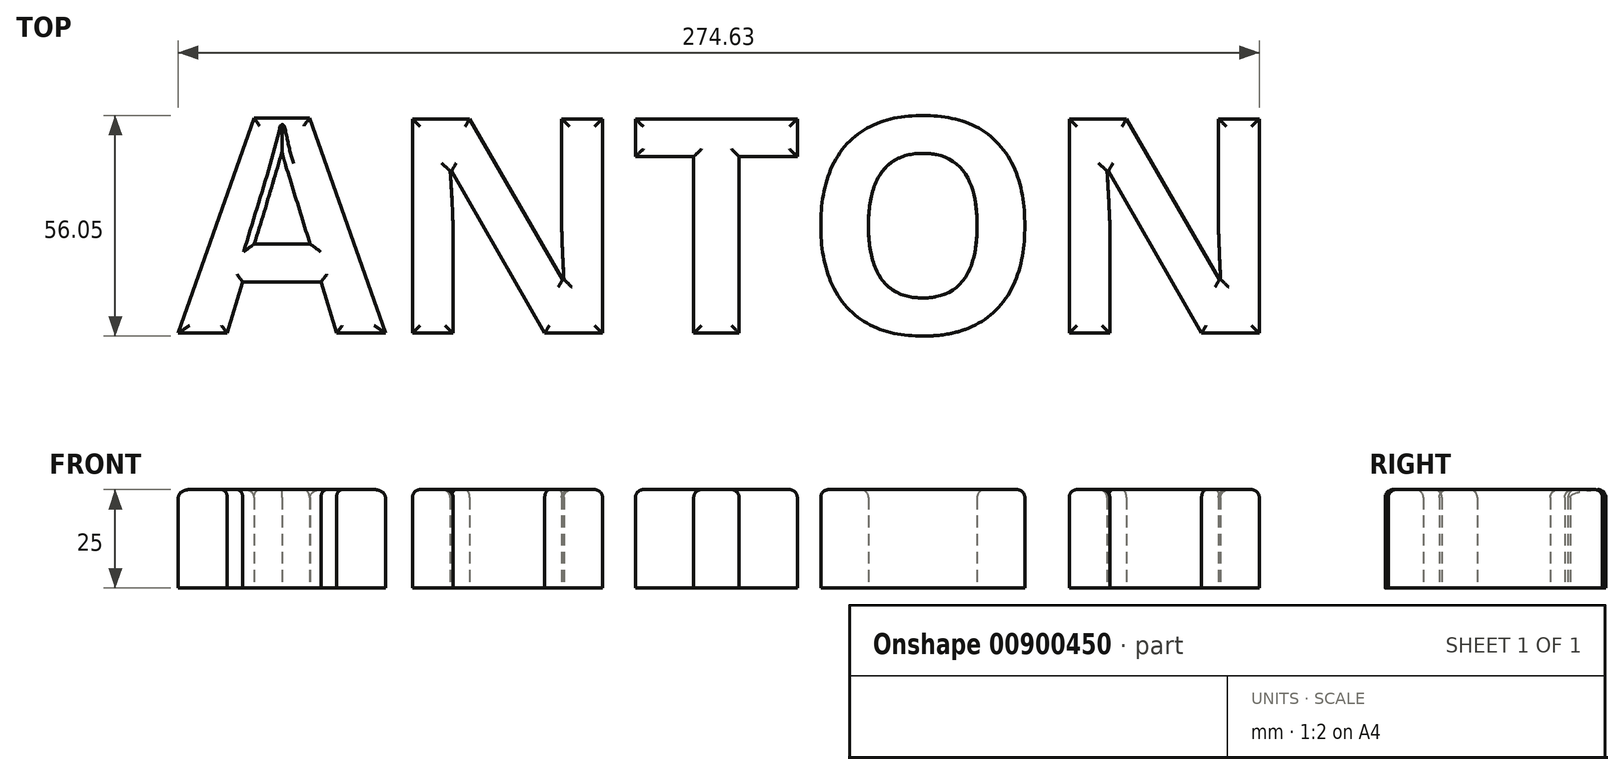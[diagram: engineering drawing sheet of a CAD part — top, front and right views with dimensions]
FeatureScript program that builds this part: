
annotation { "Feature Type Name" : "Feature", "Feature Type Description" : "" }
export const myFeature = defineFeature(function(context is Context, id is Id, definition is map)
    precondition{}
    {
        {
            var Q0;
            Q0=qCreatedBy(makeId("Top.planeOp"),FACE);
            var sketch = newSketch(context, id + "F0", { "sketchPlane" : qUnion([Q0])});
            skText(sketch, "E0", { "text": "ANTON", "fontName": "OpenSans-Bold.ttf"});
            const initialGuessF0  = {"E0": [-0.1224, -0.01433, 1, 0, 0.05491]};
            skSetInitialGuess(sketch, initialGuessF0);
            skSolve(sketch);
        }
        {
            var Q0;
            Q0 = qSketchRegion(id + "F0", true);
            extrude(context, id + "F1", {"entities" : qUnion([Q0]), "depth" : 25 * mm, "offsetDistance" : 25 * mm});
        }
        {
            var Q0;
            Q0=makeQuery(id+"F1.opExtrude","CAP_EDGE",EDGE,{"disambiguationData":[OSD([sQuery(id+"F0.wireOp",EDGE,"E0.sketch_text.stroke-49")])],"isStart":false});
            var Q1;
            Q1=makeQuery(id+"F1.opExtrude","CAP_EDGE",EDGE,{"disambiguationData":[OSD([sQuery(id+"F0.wireOp",EDGE,"E0.sketch_text.stroke-52")])],"isStart":false});
            var Q2;
            Q2=makeQuery(id+"F1.opExtrude","CAP_EDGE",EDGE,{"disambiguationData":[OSD([sQuery(id+"F0.wireOp",EDGE,"E0.sketch_text.stroke-48")])],"isStart":false});
            var Q3;
            Q3=makeQuery(id+"F1.opExtrude","CAP_EDGE",EDGE,{"disambiguationData":[OSD([sQuery(id+"F0.wireOp",EDGE,"E0.sketch_text.stroke-53")])],"isStart":false});
            var Q4;
            Q4=makeQuery(id+"F1.opExtrude","CAP_EDGE",EDGE,{"disambiguationData":[OSD([sQuery(id+"F0.wireOp",EDGE,"E0.sketch_text.stroke-36")])],"isStart":false});
            var Q5;
            Q5=makeQuery(id+"F1.opExtrude","CAP_EDGE",EDGE,{"disambiguationData":[OSD([sQuery(id+"F0.wireOp",EDGE,"E0.sketch_text.stroke-35")])],"isStart":false});
            var Q6;
            Q6=makeQuery(id+"F1.opExtrude","CAP_EDGE",EDGE,{"disambiguationData":[OSD([sQuery(id+"F0.wireOp",EDGE,"E0.sketch_text.stroke-37")])],"isStart":false});
            var Q7;
            Q7=makeQuery(id+"F1.opExtrude","CAP_EDGE",EDGE,{"disambiguationData":[OSD([sQuery(id+"F0.wireOp",EDGE,"E0.sketch_text.stroke-34")])],"isStart":false});
            var Q8;
            Q8=makeQuery(id+"F1.opExtrude","CAP_EDGE",EDGE,{"disambiguationData":[OSD([sQuery(id+"F0.wireOp",EDGE,"E0.sketch_text.stroke-25")])],"isStart":false});
            var Q9;
            Q9=makeQuery(id+"F1.opExtrude","CAP_EDGE",EDGE,{"disambiguationData":[OSD([sQuery(id+"F0.wireOp",EDGE,"E0.sketch_text.stroke-12")])],"isStart":false});
            var Q10;
            Q10=makeQuery(id+"F1.opExtrude","CAP_EDGE",EDGE,{"disambiguationData":[OSD([sQuery(id+"F0.wireOp",EDGE,"E0.sketch_text.stroke-13")])],"isStart":false});
            var Q11;
            Q11=makeQuery(id+"F1.opExtrude","CAP_EDGE",EDGE,{"disambiguationData":[OSD([sQuery(id+"F0.wireOp",EDGE,"E0.sketch_text.stroke-16")])],"isStart":false});
            var Q12;
            Q12=makeQuery(id+"F1.opExtrude","CAP_EDGE",EDGE,{"disambiguationData":[OSD([sQuery(id+"F0.wireOp",EDGE,"E0.sketch_text.stroke-17")])],"isStart":false});
            var Q13;
            Q13=makeQuery(id+"F1.opExtrude","CAP_EDGE",EDGE,{"disambiguationData":[OSD([sQuery(id+"F0.wireOp",EDGE,"E0.sketch_text.stroke-3")])],"isStart":false});
            var Q14;
            Q14=makeQuery(id+"F1.opExtrude","CAP_EDGE",EDGE,{"disambiguationData":[OSD([sQuery(id+"F0.wireOp",EDGE,"E0.sketch_text.stroke-2")])],"isStart":false});
            var Q15;
            Q15=makeQuery(id+"F1.opExtrude","CAP_EDGE",EDGE,{"disambiguationData":[OSD([sQuery(id+"F0.wireOp",EDGE,"E0.sketch_text.stroke-7")])],"isStart":false});
            var Q16;
            Q16=makeQuery(id+"F1.opExtrude","CAP_EDGE",EDGE,{"disambiguationData":[OSD([sQuery(id+"F0.wireOp",EDGE,"E0.sketch_text.stroke-0")])],"isStart":false});
            var Q17;
            Q17=makeQuery(id+"F1.opExtrude","CAP_EDGE",EDGE,{"disambiguationData":[OSD([sQuery(id+"F0.wireOp",EDGE,"E0.sketch_text.stroke-1")])],"isStart":false});
            var Q18;
            Q18=makeQuery(id+"F1.opExtrude","CAP_EDGE",EDGE,{"disambiguationData":[OSD([sQuery(id+"F0.wireOp",EDGE,"E0.sketch_text.stroke-28")])],"isStart":false});
            var Q19;
            Q19=makeQuery(id+"F1.opExtrude","CAP_EDGE",EDGE,{"disambiguationData":[OSD([sQuery(id+"F0.wireOp",EDGE,"E0.sketch_text.stroke-32")])],"isStart":false});
            var Q20;
            Q20=makeQuery(id+"F1.opExtrude","CAP_EDGE",EDGE,{"disambiguationData":[OSD([sQuery(id+"F0.wireOp",EDGE,"E0.sketch_text.stroke-26")])],"isStart":false});
            var Q21;
            Q21=makeQuery(id+"F1.opExtrude","CAP_EDGE",EDGE,{"disambiguationData":[OSD([sQuery(id+"F0.wireOp",EDGE,"E0.sketch_text.stroke-31")])],"isStart":false});
            var Q22;
            Q22=makeQuery(id+"F1.opExtrude","CAP_EDGE",EDGE,{"disambiguationData":[OSD([sQuery(id+"F0.wireOp",EDGE,"E0.sketch_text.stroke-33")])],"isStart":false});
            var Q23;
            Q23=makeQuery(id+"F1.opExtrude","CAP_EDGE",EDGE,{"disambiguationData":[OSD([sQuery(id+"F0.wireOp",EDGE,"E0.sketch_text.stroke-54")])],"isStart":false});
            var Q24;
            Q24=makeQuery(id+"F1.opExtrude","CAP_EDGE",EDGE,{"disambiguationData":[OSD([sQuery(id+"F0.wireOp",EDGE,"E0.sketch_text.stroke-51")])],"isStart":false});
            var Q25;
            Q25=makeQuery(id+"F1.opExtrude","CAP_EDGE",EDGE,{"disambiguationData":[OSD([sQuery(id+"F0.wireOp",EDGE,"E0.sketch_text.stroke-56")])],"isStart":false});
            var Q26;
            Q26=makeQuery(id+"F1.opExtrude","CAP_EDGE",EDGE,{"disambiguationData":[OSD([sQuery(id+"F0.wireOp",EDGE,"E0.sketch_text.stroke-55")])],"isStart":false});
            var Q27;
            Q27=makeQuery(id+"F1.opExtrude","CAP_EDGE",EDGE,{"disambiguationData":[OSD([sQuery(id+"F0.wireOp",EDGE,"E0.sketch_text.stroke-60")])],"isStart":false});
            var Q28;
            Q28=makeQuery(id+"F1.opExtrude","CAP_EDGE",EDGE,{"disambiguationData":[OSD([sQuery(id+"F0.wireOp",EDGE,"E0.sketch_text.stroke-61")])],"isStart":false});
            var Q29;
            Q29=makeQuery(id+"F1.opExtrude","CAP_EDGE",EDGE,{"disambiguationData":[OSD([sQuery(id+"F0.wireOp",EDGE,"E0.sketch_text.stroke-40")])],"isStart":false});
            var Q30;
            Q30=makeQuery(id+"F1.opExtrude","CAP_EDGE",EDGE,{"disambiguationData":[OSD([sQuery(id+"F0.wireOp",EDGE,"E0.sketch_text.stroke-43")])],"isStart":false});
            var Q31;
            Q31=makeQuery(id+"F1.opExtrude","CAP_EDGE",EDGE,{"disambiguationData":[OSD([sQuery(id+"F0.wireOp",EDGE,"E0.sketch_text.stroke-38")])],"isStart":false});
            var Q32;
            Q32=makeQuery(id+"F1.opExtrude","CAP_EDGE",EDGE,{"disambiguationData":[OSD([sQuery(id+"F0.wireOp",EDGE,"E0.sketch_text.stroke-39")])],"isStart":false});
            var Q33;
            Q33=makeQuery(id+"F1.opExtrude","CAP_EDGE",EDGE,{"disambiguationData":[OSD([sQuery(id+"F0.wireOp",EDGE,"E0.sketch_text.stroke-42")])],"isStart":false});
            var Q34;
            Q34=makeQuery(id+"F1.opExtrude","CAP_EDGE",EDGE,{"disambiguationData":[OSD([sQuery(id+"F0.wireOp",EDGE,"E0.sketch_text.stroke-41")])],"isStart":false});
            var Q35;
            Q35=makeQuery(id+"F1.opExtrude","CAP_EDGE",EDGE,{"disambiguationData":[OSD([sQuery(id+"F0.wireOp",EDGE,"E0.sketch_text.stroke-44")])],"isStart":false});
            var Q36;
            Q36=makeQuery(id+"F1.opExtrude","CAP_EDGE",EDGE,{"disambiguationData":[OSD([sQuery(id+"F0.wireOp",EDGE,"E0.sketch_text.stroke-24")])],"isStart":false});
            var Q37;
            Q37=makeQuery(id+"F1.opExtrude","CAP_EDGE",EDGE,{"disambiguationData":[OSD([sQuery(id+"F0.wireOp",EDGE,"E0.sketch_text.stroke-20")])],"isStart":false});
            var Q38;
            Q38=makeQuery(id+"F1.opExtrude","CAP_EDGE",EDGE,{"disambiguationData":[OSD([sQuery(id+"F0.wireOp",EDGE,"E0.sketch_text.stroke-15")])],"isStart":false});
            var Q39;
            Q39=makeQuery(id+"F1.opExtrude","CAP_EDGE",EDGE,{"disambiguationData":[OSD([sQuery(id+"F0.wireOp",EDGE,"E0.sketch_text.stroke-18")])],"isStart":false});
            var Q40;
            Q40=makeQuery(id+"F1.opExtrude","CAP_EDGE",EDGE,{"disambiguationData":[OSD([sQuery(id+"F0.wireOp",EDGE,"E0.sketch_text.stroke-19")])],"isStart":false});
            var Q41;
            Q41=makeQuery(id+"F1.opExtrude","CAP_EDGE",EDGE,{"disambiguationData":[OSD([sQuery(id+"F0.wireOp",EDGE,"E0.sketch_text.stroke-11")])],"isStart":false});
            var Q42;
            Q42=makeQuery(id+"F1.opExtrude","CAP_EDGE",EDGE,{"disambiguationData":[OSD([sQuery(id+"F0.wireOp",EDGE,"E0.sketch_text.stroke-10")])],"isStart":false});
            var Q43;
            Q43=makeQuery(id+"F1.opExtrude","CAP_EDGE",EDGE,{"disambiguationData":[OSD([sQuery(id+"F0.wireOp",EDGE,"E0.sketch_text.stroke-8")])],"isStart":false});
            var Q44;
            Q44=makeQuery(id+"F1.opExtrude","CAP_EDGE",EDGE,{"disambiguationData":[OSD([sQuery(id+"F0.wireOp",EDGE,"E0.sketch_text.stroke-6")])],"isStart":false});
            var Q45;
            Q45=makeQuery(id+"F1.opExtrude","CAP_EDGE",EDGE,{"disambiguationData":[OSD([sQuery(id+"F0.wireOp",EDGE,"E0.sketch_text.stroke-4")])],"isStart":false});
            var Q46;
            Q46=makeQuery(id+"F1.opExtrude","CAP_EDGE",EDGE,{"disambiguationData":[OSD([sQuery(id+"F0.wireOp",EDGE,"E0.sketch_text.stroke-27")])],"isStart":false});
            var Q47;
            Q47=makeQuery(id+"F1.opExtrude","CAP_EDGE",EDGE,{"disambiguationData":[OSD([sQuery(id+"F0.wireOp",EDGE,"E0.sketch_text.stroke-29")])],"isStart":false});
            var Q48;
            Q48=makeQuery(id+"F1.opExtrude","CAP_EDGE",EDGE,{"disambiguationData":[OSD([sQuery(id+"F0.wireOp",EDGE,"E0.sketch_text.stroke-30")])],"isStart":false});
            var Q49;
            Q49=makeQuery(id+"F1.opExtrude","CAP_EDGE",EDGE,{"disambiguationData":[OSD([sQuery(id+"F0.wireOp",EDGE,"E0.sketch_text.stroke-50")])],"isStart":false});
            var Q50;
            Q50=makeQuery(id+"F1.opExtrude","CAP_EDGE",EDGE,{"disambiguationData":[OSD([sQuery(id+"F0.wireOp",EDGE,"E0.sketch_text.stroke-58")])],"isStart":false});
            var Q51;
            Q51=makeQuery(id+"F1.opExtrude","CAP_EDGE",EDGE,{"disambiguationData":[OSD([sQuery(id+"F0.wireOp",EDGE,"E0.sketch_text.stroke-57")])],"isStart":false});
            var Q52;
            Q52=makeQuery(id+"F1.opExtrude","CAP_EDGE",EDGE,{"disambiguationData":[OSD([sQuery(id+"F0.wireOp",EDGE,"E0.sketch_text.stroke-46")])],"isStart":false});
            var Q53;
            Q53=makeQuery(id+"F1.opExtrude","CAP_EDGE",EDGE,{"disambiguationData":[OSD([sQuery(id+"F0.wireOp",EDGE,"E0.sketch_text.stroke-45")])],"isStart":false});
            var Q54;
            Q54=makeQuery(id+"F1.opExtrude","CAP_EDGE",EDGE,{"disambiguationData":[OSD([sQuery(id+"F0.wireOp",EDGE,"E0.sketch_text.stroke-47")])],"isStart":false});
            var Q55;
            Q55=makeQuery(id+"F1.opExtrude","CAP_EDGE",EDGE,{"disambiguationData":[OSD([sQuery(id+"F0.wireOp",EDGE,"E0.sketch_text.stroke-21")])],"isStart":false});
            var Q56;
            Q56=makeQuery(id+"F1.opExtrude","CAP_EDGE",EDGE,{"disambiguationData":[OSD([sQuery(id+"F0.wireOp",EDGE,"E0.sketch_text.stroke-14")])],"isStart":false});
            var Q57;
            Q57=makeQuery(id+"F1.opExtrude","CAP_EDGE",EDGE,{"disambiguationData":[OSD([sQuery(id+"F0.wireOp",EDGE,"E0.sketch_text.stroke-23")])],"isStart":false});
            var Q58;
            Q58=makeQuery(id+"F1.opExtrude","CAP_EDGE",EDGE,{"disambiguationData":[OSD([sQuery(id+"F0.wireOp",EDGE,"E0.sketch_text.stroke-5")])],"isStart":false});
            var Q59;
            Q59=makeQuery(id+"F1.opExtrude","CAP_EDGE",EDGE,{"disambiguationData":[OSD([sQuery(id+"F0.wireOp",EDGE,"E0.sketch_text.stroke-9")])],"isStart":false});
            var Q60;
            Q60=makeQuery(id+"F1.opExtrude","CAP_EDGE",EDGE,{"disambiguationData":[OSD([sQuery(id+"F0.wireOp",EDGE,"E0.sketch_text.stroke-59")])],"isStart":false});
            var Q61;
            Q61=makeQuery(id+"F1.opExtrude","CAP_EDGE",EDGE,{"disambiguationData":[OSD([sQuery(id+"F0.wireOp",EDGE,"E0.sketch_text.stroke-22")])],"isStart":false});
            fillet(context, id + "F2", {"entities" : qUnion([Q0, Q1, Q2, Q3, Q4, Q5, Q6, Q7, Q8, Q9, Q10, Q11, Q12, Q13, Q14, Q15, Q16, Q17, Q18, Q19, Q20, Q21, Q22, Q23, Q24, Q25, Q26, Q27, Q28, Q29, Q30, Q31, Q32, Q33, Q34, Q35, Q36, Q37, Q38, Q39, Q40, Q41, Q42, Q43, Q44, Q45, Q46, Q47, Q48, Q49, Q50, Q51, Q52, Q53, Q54, Q55, Q56, Q57, Q58, Q59, Q60, Q61]), "radius" : 2 * mm, "tangentPropagation" : true, "allowEdgeOverflow" : false});
        }
    });
